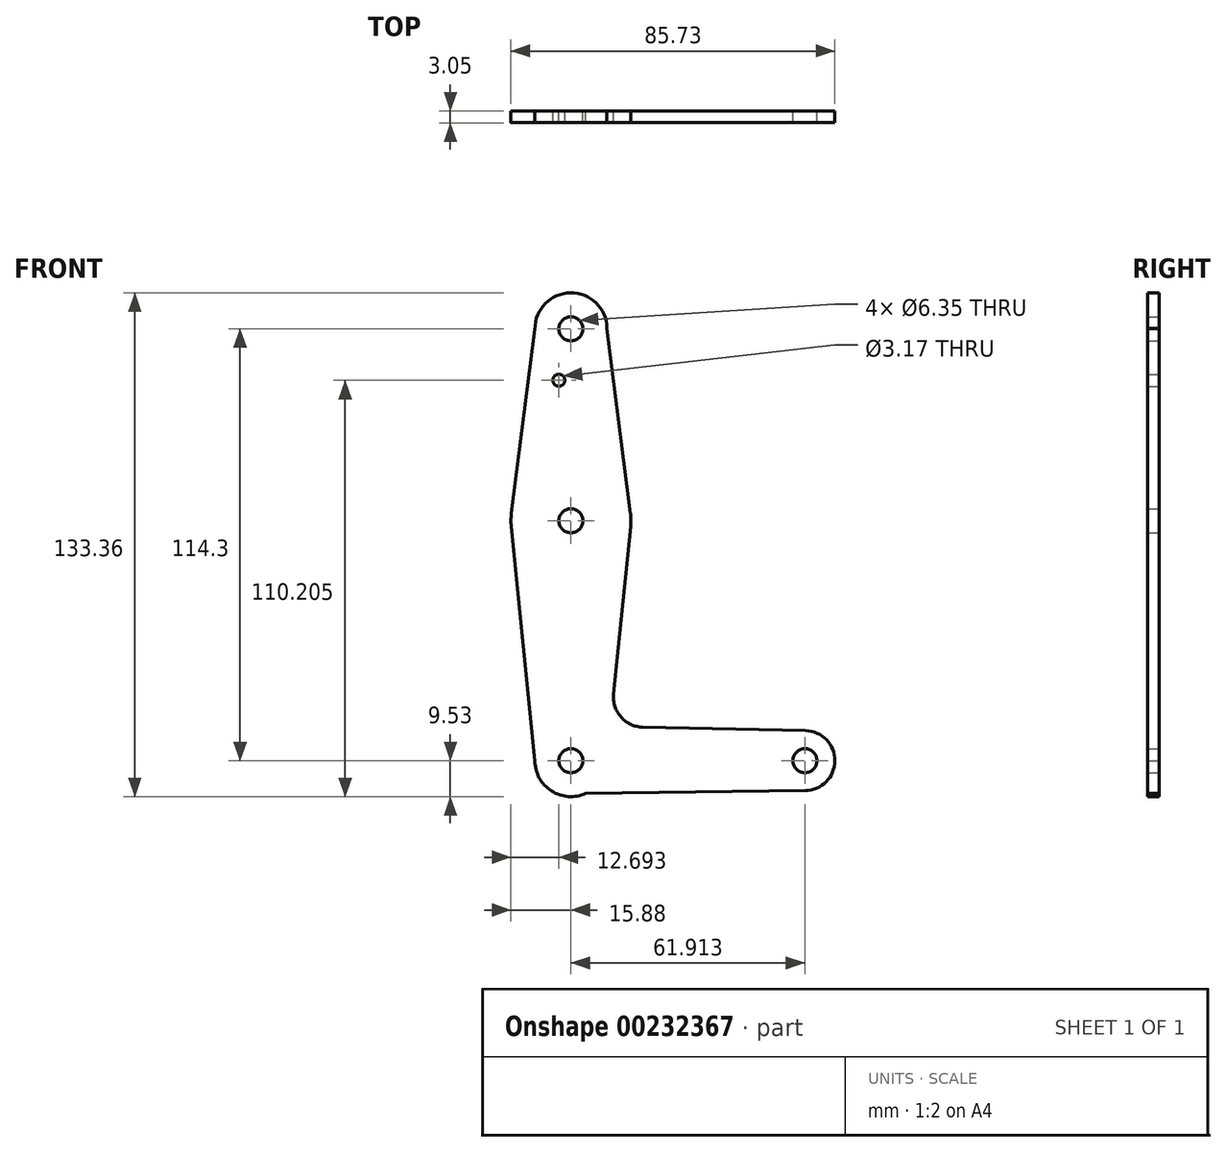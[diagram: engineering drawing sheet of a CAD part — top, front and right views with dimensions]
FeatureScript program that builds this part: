
annotation { "Feature Type Name" : "Feature", "Feature Type Description" : "" }
export const myFeature = defineFeature(function(context is Context, id is Id, definition is map)
    precondition{}
    {
        {
            var Q0;
            Q0=qCreatedBy(makeId("Front.planeOp"),FACE);
            var sketch = newSketch(context, id + "F0", { "sketchPlane" : qUnion([Q0])});
            skLineSegment(sketch, "E0", {"start": v(0, 114.3) * mm, "end": v(0, 63.5) * mm});
            skLineSegment(sketch, "E1", {"start": v(0, 114.3) * mm, "end": v(0, 0) * mm});
            skLineSegment(sketch, "E2", {"start": v(0, 0) * mm, "end": v(61.91, 0) * mm});
            skCircle(sketch, "E3", {"center": v(0, 63.5) * mm, "radius": 15.88 * mm});
            skCircle(sketch, "E4", {"center": v(0, 114.3) * mm, "radius": 9.53 * mm});
            skCircle(sketch, "E5", {"center": v(61.91, 0) * mm, "radius": 7.94 * mm});
            skCircle(sketch, "E6", {"center": v(0, 0) * mm, "radius": 9.53 * mm});
            skLineSegment(sketch, "E7", {"start": v(-9.52, 114.2) * mm, "end": v(-15.75, 65.51) * mm});
            skLineSegment(sketch, "E8", {"start": v(-9.53, 0) * mm, "end": v(-15.8, 61.9) * mm});
            skLineSegment(sketch, "E9", {"start": v(9.52, 114.47) * mm, "end": v(15.75, 65.5) * mm});
            skLineSegment(sketch, "E10", {"start": v(11.3, 17.61) * mm, "end": v(15.8, 61.9) * mm});
            skLineSegment(sketch, "E11", {"start": v(19.05, 8.86) * mm, "end": v(62.08, 7.94) * mm});
            skLineSegment(sketch, "E12", {"start": v(3.94, -8.67) * mm, "end": v(62.01, -7.94) * mm});
            skCircle(sketch, "E13", {"center": v(0, 114.3) * mm, "radius": 3.18 * mm});
            skCircle(sketch, "E14", {"center": v(0, 63.5) * mm, "radius": 3.18 * mm});
            skCircle(sketch, "E15", {"center": v(0, 0) * mm, "radius": 3.18 * mm});
            skCircle(sketch, "E16", {"center": v(61.91, 0) * mm, "radius": 3.18 * mm});
            skCircle(sketch, "E17", {"center": v(-3.19, 100.67) * mm, "radius": 1.59 * mm});
            skArc(sketch, "E18.filletArc", {"start": v(11.3, 17.61) * mm, "mid": v(13.26, 11.54) * mm, "end": v(19.05, 8.86) * mm});
            skSolve(sketch);
        }
        {
            var Q0;
            Q0 = qSketchRegion(id + "F0", true);
            var Q1;
            {var subQ0=sQuery(id+"F0.wireOp",EDGE,"E15");var subQ1=sQuery(id+"F0.wireOp",EDGE,"E2");var subQ2=makeQuery(id+"F0.imprint","INTERSECT",VERTEX,{"derivedFrom":[subQ1,subQ0]});Q1=makeQuery(id+"F0.imprint","IMPRINT",FACE,{"disambiguationData":[TD([[makeQuery(id+"F0.imprint","IMPRINT",EDGE,{"disambiguationData":[TD([[subQ2,-1.0]])],"derivedFrom":subQ1}),1.0]])]});}
            extrude(context, id + "F1", {"entities" : qUnion([Q0, Q1]), "depth" : 3.05 * mm});
        }
    });
